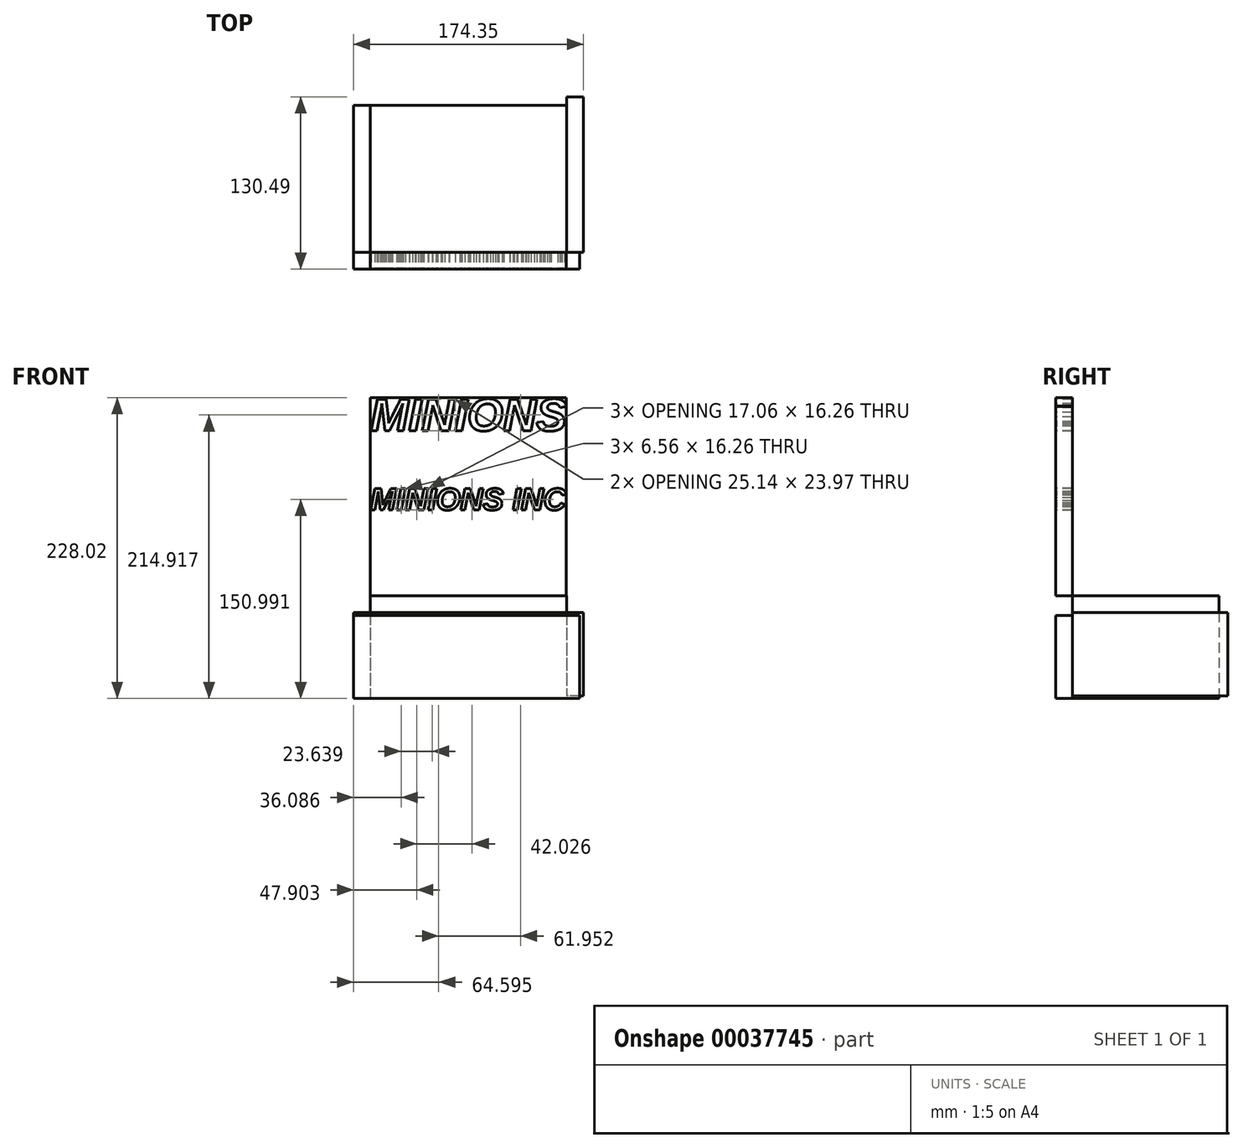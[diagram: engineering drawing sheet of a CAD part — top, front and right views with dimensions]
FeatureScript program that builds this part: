
annotation { "Feature Type Name" : "Feature", "Feature Type Description" : "" }
export const myFeature = defineFeature(function(context is Context, id is Id, definition is map)
    precondition{}
    {
        {
            var Q0;
            Q0=qCreatedBy(makeId("Front.planeOp"),FACE);
            var sketch = newSketch(context, id + "F0", { "sketchPlane" : qUnion([Q0])});
            skLineSegment(sketch, "E0.bottom", {"start": v(-73.55, 74.44) * mm, "end": v(75.15, 74.44) * mm});
            skLineSegment(sketch, "E0.top", {"start": v(-73.55, -75.58) * mm, "end": v(75.15, -75.58) * mm});
            skLineSegment(sketch, "E0.left", {"start": v(-73.55, 74.44) * mm, "end": v(-73.55, -75.58) * mm});
            skLineSegment(sketch, "E0.right", {"start": v(75.15, 74.44) * mm, "end": v(75.15, -75.58) * mm});
            skSolve(sketch);
        }
        {
            var Q0;
            Q0 = qSketchRegion(id + "F0", true);
            extrude(context, id + "F1", {"entities" : qUnion([Q0]), "depth" : 12.7 * mm});
        }
        {
            var Q0;
            Q0=makeQuery(id+"F1.opExtrude","SWEPT_FACE",FACE,{"disambiguationData":[OSD([sQuery(id+"F0.wireOp",EDGE,"E0.top")])]});
            var sketch = newSketch(context, id + "F2", { "sketchPlane" : qUnion([Q0])});
            skLineSegment(sketch, "E1.bottom", {"start": v(-73.55, 0) * mm, "end": v(75.4, 0) * mm});
            skLineSegment(sketch, "E1.top", {"start": v(-73.55, -111.34) * mm, "end": v(75.4, -111.34) * mm});
            skLineSegment(sketch, "E1.left", {"start": v(-73.55, 0) * mm, "end": v(-73.55, -111.34) * mm});
            skLineSegment(sketch, "E1.right", {"start": v(75.4, 0) * mm, "end": v(75.4, -111.34) * mm});
            skSolve(sketch);
        }
        {
            var Q0;
            Q0 = qSketchRegion(id + "F2", true);
            extrude(context, id + "F3", {"entities" : qUnion([Q0]), "depth" : 12.7 * mm});
        }
        {
            var Q0;
            Q0=makeQuery(id+"F1.opExtrude","CAP_FACE",FACE,{"disambiguationData":[OSD([sQuery(id+"F0.wireOp",EDGE,"E0.bottom"),sQuery(id+"F0.wireOp",EDGE,"E0.top"),sQuery(id+"F0.wireOp",EDGE,"E0.left"),sQuery(id+"F0.wireOp",EDGE,"E0.right")])],"isStart":false});
            var sketch = newSketch(context, id + "F4", { "sketchPlane" : qUnion([Q0])});
            skText(sketch, "E2", { "text": "MINIONS", "fontName": "Arimo-BoldItalic.ttf"});
            const initialGuessF4  = {"E2": [-0.07355, 0.04935, 1, 0, 0.02509]};
            skSetInitialGuess(sketch, initialGuessF4);
            skSolve(sketch);
        }
        {
            var Q0;
            Q0 = qSketchRegion(id + "F4", true);
            extrude(context, id + "F5", {"entities" : qUnion([Q0]), "operationType" : NewBodyOperationType.REMOVE, "oppositeDirection" : true, "depth" : 25.4 * mm});
        }
        {
            var Q0;
            Q0=makeQuery(id+"F1.opExtrude","CAP_FACE",FACE,{"disambiguationData":[OSD([sQuery(id+"F0.wireOp",EDGE,"E0.bottom"),sQuery(id+"F0.wireOp",EDGE,"E0.top"),sQuery(id+"F0.wireOp",EDGE,"E0.left"),sQuery(id+"F0.wireOp",EDGE,"E0.right")])],"isStart":false});
            var sketch = newSketch(context, id + "F6", { "sketchPlane" : qUnion([Q0])});
            skText(sketch, "E3", { "text": "MINIONS", "fontName": "Arimo-BoldItalic.ttf"});
            const initialGuessF6  = {"E3": [-0.07355, 0.04935, 1, 0, 0.02509]};
            skSetInitialGuess(sketch, initialGuessF6);
            skSolve(sketch);
        }
        {
            var Q0;
            Q0 = qSketchRegion(id + "F6", true);
            extrude(context, id + "F7", {"entities" : qUnion([Q0]), "operationType" : NewBodyOperationType.REMOVE, "oppositeDirection" : true, "depth" : 25.4 * mm});
        }
        {
            var Q0;
            Q0=makeQuery(id+"F3.opExtrude","SWEPT_FACE",FACE,{"disambiguationData":[OSD([sQuery(id+"F2.wireOp",EDGE,"E1.right")])]});
            var sketch = newSketch(context, id + "F8", { "sketchPlane" : qUnion([Q0])});
            skLineSegment(sketch, "E4.bottom", {"start": v(0, -88.28) * mm, "end": v(117.79, -88.28) * mm});
            skLineSegment(sketch, "E4.top", {"start": v(0, -151.47) * mm, "end": v(117.79, -151.47) * mm});
            skLineSegment(sketch, "E4.left", {"start": v(0, -88.28) * mm, "end": v(0, -151.47) * mm});
            skLineSegment(sketch, "E4.right", {"start": v(117.79, -88.28) * mm, "end": v(117.79, -151.47) * mm});
            skSolve(sketch);
        }
        {
            var Q0;
            Q0 = qSketchRegion(id + "F8", true);
            extrude(context, id + "F9", {"entities" : qUnion([Q0]), "depth" : 12.7 * mm});
        }
        {
            var Q0;
            Q0=makeQuery(id+"F3.opExtrude","SWEPT_FACE",FACE,{"disambiguationData":[OSD([sQuery(id+"F2.wireOp",EDGE,"E1.left")])]});
            var sketch = newSketch(context, id + "F10", { "sketchPlane" : qUnion([Q0])});
            skLineSegment(sketch, "E5.bottom", {"start": v(-111.34, -88.28) * mm, "end": v(-0.73, -88.28) * mm});
            skLineSegment(sketch, "E5.top", {"start": v(-111.34, -138.48) * mm, "end": v(-0.73, -138.48) * mm});
            skLineSegment(sketch, "E5.left", {"start": v(-111.34, -88.28) * mm, "end": v(-111.34, -138.48) * mm});
            skLineSegment(sketch, "E5.right", {"start": v(-0.73, -88.28) * mm, "end": v(-0.73, -138.48) * mm});
            skSolve(sketch);
        }
        {
            var Q0;
            Q0 = qSketchRegion(id + "F10", true);
            extrude(context, id + "F11", {"entities" : qUnion([Q0]), "depth" : 12.7 * mm});
        }
        {
            var Q0;
            Q0=makeQuery(id+"F11.opExtrude","SWEPT_BODY",BODY,{"disambiguationData":[OSD([sQuery(id+"F10.wireOp",EDGE,"E5.bottom"),sQuery(id+"F10.wireOp",EDGE,"E5.top"),sQuery(id+"F10.wireOp",EDGE,"E5.left"),sQuery(id+"F10.wireOp",EDGE,"E5.right")])]});
            deleteBodies(context, id + "F12", {"entities" : qUnion([Q0])});
        }
        {
            var Q0;
            Q0=makeQuery(id+"F9.opExtrude","CAP_FACE",FACE,{"disambiguationData":[OSD([sQuery(id+"F8.wireOp",EDGE,"E4.bottom"),sQuery(id+"F8.wireOp",EDGE,"E4.top"),sQuery(id+"F8.wireOp",EDGE,"E4.left"),sQuery(id+"F8.wireOp",EDGE,"E4.right")])],"isStart":true});
            var sketch = newSketch(context, id + "F13", { "sketchPlane" : qUnion([Q0])});
            skLineSegment(sketch, "E6.bottom", {"start": v(0, -88.28) * mm, "end": v(-117.79, -88.28) * mm});
            skLineSegment(sketch, "E6.top", {"start": v(0, -151.47) * mm, "end": v(-117.79, -151.47) * mm});
            skLineSegment(sketch, "E6.left", {"start": v(0, -88.28) * mm, "end": v(0, -151.47) * mm});
            skLineSegment(sketch, "E6.right", {"start": v(-117.79, -88.28) * mm, "end": v(-117.79, -151.47) * mm});
            skSolve(sketch);
        }
        {
            var Q0;
            Q0 = qSketchRegion(id + "F13", true);
            extrude(context, id + "F14", {"entities" : qUnion([Q0]), "depth" : 12.7 * mm});
        }
        {
            var Q0;
            Q0=makeQuery(id+"F14.opExtrude","SWEPT_BODY",BODY,{"disambiguationData":[OSD([sQuery(id+"F13.wireOp",EDGE,"E6.bottom"),sQuery(id+"F13.wireOp",EDGE,"E6.top"),sQuery(id+"F13.wireOp",EDGE,"E6.left"),sQuery(id+"F13.wireOp",EDGE,"E6.right")])]});
            deleteBodies(context, id + "F15", {"entities" : qUnion([Q0])});
        }
        {
            var Q0;
            Q0=makeQuery(id+"F3.opExtrude","SWEPT_FACE",FACE,{"disambiguationData":[OSD([sQuery(id+"F2.wireOp",EDGE,"E1.left")])]});
            var sketch = newSketch(context, id + "F16", { "sketchPlane" : qUnion([Q0])});
            skPoint(sketch, "E7.oppositeSnap0", {"position": v(-111.34, -81.93) * mm});
            skLineSegment(sketch, "E7.bottom", {"start": v(0, -88.28) * mm, "end": v(-111.34, -88.28) * mm});
            skLineSegment(sketch, "E7.top", {"start": v(0, -153.58) * mm, "end": v(-111.34, -153.58) * mm});
            skLineSegment(sketch, "E7.left", {"start": v(0, -88.28) * mm, "end": v(0, -153.58) * mm});
            skLineSegment(sketch, "E7.right", {"start": v(-111.34, -88.28) * mm, "end": v(-111.34, -153.58) * mm});
            skSolve(sketch);
        }
        {
            var Q0;
            Q0 = qSketchRegion(id + "F16", true);
            extrude(context, id + "F17", {"entities" : qUnion([Q0]), "depth" : 12.7 * mm});
        }
        {
            var Q0;
            Q0=makeQuery(id+"F17.opExtrude","SWEPT_FACE",FACE,{"disambiguationData":[OSD([sQuery(id+"F16.wireOp",EDGE,"E7.left")])]});
            var sketch = newSketch(context, id + "F18", { "sketchPlane" : qUnion([Q0])});
            skLineSegment(sketch, "E8.bottom", {"start": v(-86.25, -153.58) * mm, "end": v(85.25, -153.58) * mm});
            skLineSegment(sketch, "E8.top", {"start": v(-86.25, -90.53) * mm, "end": v(85.25, -90.53) * mm});
            skLineSegment(sketch, "E8.left", {"start": v(-86.25, -153.58) * mm, "end": v(-86.25, -90.53) * mm});
            skLineSegment(sketch, "E8.right", {"start": v(85.25, -153.58) * mm, "end": v(85.25, -90.53) * mm});
            skSolve(sketch);
        }
        {
            var Q0;
            Q0 = qSketchRegion(id + "F18", true);
            extrude(context, id + "F19", {"entities" : qUnion([Q0]), "depth" : 12.7 * mm});
        }
        {
            var Q0;
            Q0=makeQuery(id+"F1.opExtrude","CAP_FACE",FACE,{"disambiguationData":[OSD([sQuery(id+"F0.wireOp",EDGE,"E0.bottom"),sQuery(id+"F0.wireOp",EDGE,"E0.top"),sQuery(id+"F0.wireOp",EDGE,"E0.left"),sQuery(id+"F0.wireOp",EDGE,"E0.right")])],"isStart":false});
            var sketch = newSketch(context, id + "F20", { "sketchPlane" : qUnion([Q0])});
            skText(sketch, "E9", { "text": "MINIONS INC", "fontName": "Arimo-BoldItalic.ttf"});
            const initialGuessF20  = {"E9": [-0.07355, -0.01072, 1, 0, 0.01702]};
            skSetInitialGuess(sketch, initialGuessF20);
            skSolve(sketch);
        }
        {
            var Q0;
            Q0 = qSketchRegion(id + "F20", true);
            extrude(context, id + "F21", {"entities" : qUnion([Q0]), "operationType" : NewBodyOperationType.REMOVE, "oppositeDirection" : true, "depth" : 25.4 * mm});
        }
    });
